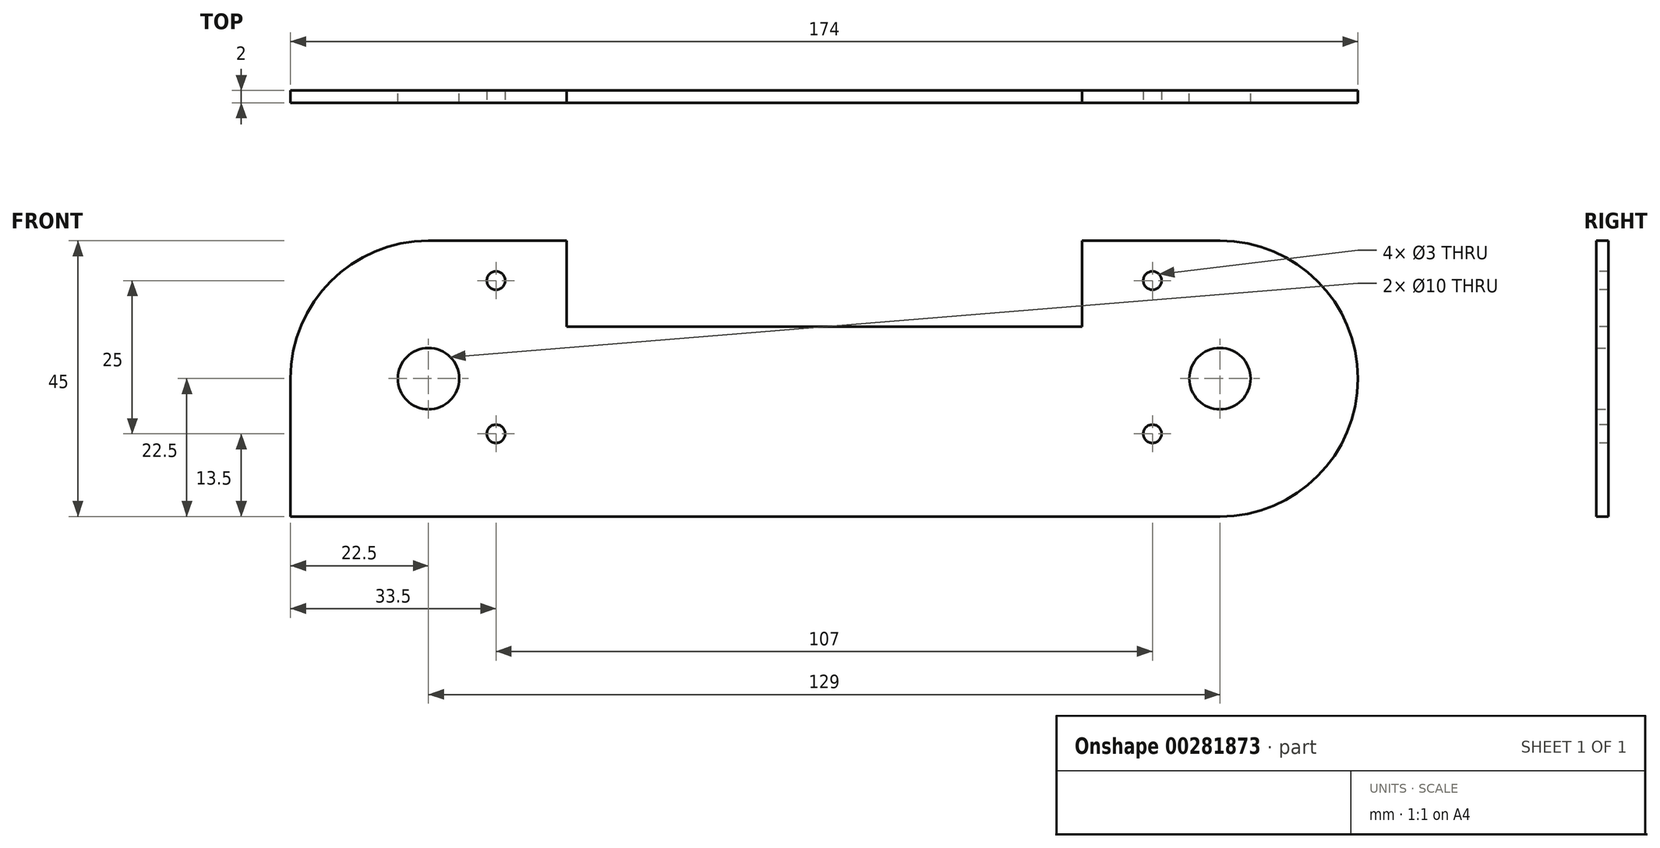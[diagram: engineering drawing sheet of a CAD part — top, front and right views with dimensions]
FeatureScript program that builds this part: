
annotation { "Feature Type Name" : "Feature", "Feature Type Description" : "" }
export const myFeature = defineFeature(function(context is Context, id is Id, definition is map)
    precondition{}
    {
        {
            var Q0;
            Q0=qCreatedBy(makeId("Front.planeOp"),FACE);
            var sketch = newSketch(context, id + "F0", { "sketchPlane" : qUnion([Q0])});
            skLineSegment(sketch, "E0.bottom", {"start": v(64.5, 22.5) * mm, "end": v(-64.5, 22.5) * mm});
            skLineSegment(sketch, "E0.top", {"start": v(64.5, -22.5) * mm, "end": v(-64.5, -22.5) * mm});
            skPoint(sketch, "E0.middle", {"position": v(0, 0) * mm});
            skCircle(sketch, "E1", {"center": v(64.5, 0) * mm, "radius": 5 * mm});
            skCircle(sketch, "E2", {"center": v(-64.5, 0) * mm, "radius": 5 * mm});
            skArc(sketch, "E3", {"start": v(-64.5, 22.5) * mm, "mid": v(-87, 0) * mm, "end": v(-64.5, -22.5) * mm});
            skArc(sketch, "E4", {"start": v(64.5, -22.5) * mm, "mid": v(87, 0) * mm, "end": v(64.5, 22.5) * mm});
            skPoint(sketch, "E5.orphan", {"position": v(-81.5, 22.5) * mm});
            skPoint(sketch, "E6.orphan", {"position": v(-81.5, -22.5) * mm});
            skPoint(sketch, "E7.orphan", {"position": v(81.5, 22.5) * mm});
            skPoint(sketch, "E8.orphan", {"position": v(81.5, -22.5) * mm});
            skSolve(sketch);
        }
        {
            var Q0;
            Q0=qSketchRegion(id+"F0",true);
            extrude(context, id + "F1", {"entities" : qUnion([Q0]), "depth" : 2 * mm});
        }
        {
            var Q0;
            Q0=makeQuery(id+"F1.opExtrude","CAP_FACE",FACE,{"disambiguationData":[OSD([sQuery(id+"F0.wireOp",EDGE,"E0.bottom"),sQuery(id+"F0.wireOp",EDGE,"E0.top"),sQuery(id+"F0.wireOp",EDGE,"E1"),sQuery(id+"F0.wireOp",EDGE,"E2"),sQuery(id+"F0.wireOp",EDGE,"E3"),sQuery(id+"F0.wireOp",EDGE,"E4")])],"isStart":false});
            var sketch = newSketch(context, id + "F2", { "sketchPlane" : qUnion([Q0])});
            skLineSegment(sketch, "E9.top", {"start": v(-64.5, -22.5) * mm, "end": v(-87, -22.5) * mm});
            skLineSegment(sketch, "E9.right", {"start": v(-87, 0) * mm, "end": v(-87, -22.5) * mm});
            skPoint(sketch, "E9.left.start.orphan", {"position": v(-64.5, 0) * mm});
            skLineSegment(sketch, "E10", {"start": v(-87, 0) * mm, "end": v(-80.88, 0) * mm});
            skLineSegment(sketch, "E11", {"start": v(-80.88, 0) * mm, "end": v(-78.27, -9.46) * mm});
            skLineSegment(sketch, "E12", {"start": v(-78.27, -9.46) * mm, "end": v(-70.55, -14.76) * mm});
            skLineSegment(sketch, "E13", {"start": v(-70.55, -14.76) * mm, "end": v(-64.5, -17.43) * mm});
            skLineSegment(sketch, "E14", {"start": v(-64.5, -17.43) * mm, "end": v(-64.5, -22.5) * mm});
            skSolve(sketch);
        }
        {
            var Q0;
            Q0=qSketchRegion(id+"F2",true);
            extrude(context, id + "F3", {"entities" : qUnion([Q0]), "operationType" : NewBodyOperationType.ADD, "oppositeDirection" : true, "depth" : 2 * mm});
        }
        {
            var Q0;
            Q0=makeQuery(id+"F3.boolean.opBoolean","MERGE",FACE,{"derivedFrom":[makeQuery(id+"F1.opExtrude","CAP_FACE",FACE,{"disambiguationData":[OSD([sQuery(id+"F0.wireOp",EDGE,"E0.bottom"),sQuery(id+"F0.wireOp",EDGE,"E0.top"),sQuery(id+"F0.wireOp",EDGE,"E1"),sQuery(id+"F0.wireOp",EDGE,"E2"),sQuery(id+"F0.wireOp",EDGE,"E3"),sQuery(id+"F0.wireOp",EDGE,"E4")])],"isStart":false}),makeQuery(id+"F3.opExtrude","CAP_FACE",FACE,{"disambiguationData":[OSD([sQuery(id+"F2.wireOp",EDGE,"E9.top"),sQuery(id+"F2.wireOp",EDGE,"E9.right"),sQuery(id+"F2.wireOp",EDGE,"E10"),sQuery(id+"F2.wireOp",EDGE,"E11"),sQuery(id+"F2.wireOp",EDGE,"E12"),sQuery(id+"F2.wireOp",EDGE,"E13"),sQuery(id+"F2.wireOp",EDGE,"E14")])],"isStart":true})]});
            var sketch = newSketch(context, id + "F4", { "sketchPlane" : qUnion([Q0])});
            skLineSegment(sketch, "E15.bottom", {"start": v(47, 22.5) * mm, "end": v(-47, 22.5) * mm, "construction": true});
            skLineSegment(sketch, "E15.top", {"start": v(47, -22.5) * mm, "end": v(-47, -22.5) * mm, "construction": true});
            skLineSegment(sketch, "E15.left", {"start": v(47, 22.5) * mm, "end": v(47, -22.5) * mm, "construction": true});
            skLineSegment(sketch, "E15.right", {"start": v(-47, 22.5) * mm, "end": v(-47, -22.5) * mm, "construction": true});
            skPoint(sketch, "E15.middle", {"position": v(0, 0) * mm});
            skLineSegment(sketch, "E16", {"start": v(-59.5, 0) * mm, "end": v(59.5, 0) * mm, "construction": true});
            skCircle(sketch, "E17", {"center": v(-53.5, 16) * mm, "radius": 1.5 * mm});
            skCircle(sketch, "E18", {"center": v(-53.5, -9) * mm, "radius": 1.5 * mm});
            skCircle(sketch, "E19", {"center": v(53.5, 16) * mm, "radius": 1.5 * mm});
            skCircle(sketch, "E20", {"center": v(53.5, -9) * mm, "radius": 1.5 * mm});
            skSolve(sketch);
        }
        {
            var Q0;
            Q0=qSketchRegion(id+"F4",true);
            extrude(context, id + "F5", {"entities" : qUnion([Q0]), "operationType" : NewBodyOperationType.REMOVE, "oppositeDirection" : true, "depth" : 25 * mm});
        }
        {
            var Q0;
            Q0=makeQuery(id+"F3.boolean.opBoolean","MERGE",FACE,{"derivedFrom":[makeQuery(id+"F1.opExtrude","CAP_FACE",FACE,{"disambiguationData":[OSD([sQuery(id+"F0.wireOp",EDGE,"E0.bottom"),sQuery(id+"F0.wireOp",EDGE,"E0.top"),sQuery(id+"F0.wireOp",EDGE,"E1"),sQuery(id+"F0.wireOp",EDGE,"E2"),sQuery(id+"F0.wireOp",EDGE,"E3"),sQuery(id+"F0.wireOp",EDGE,"E4")])],"isStart":false}),makeQuery(id+"F3.opExtrude","CAP_FACE",FACE,{"disambiguationData":[OSD([sQuery(id+"F2.wireOp",EDGE,"E9.top"),sQuery(id+"F2.wireOp",EDGE,"E9.right"),sQuery(id+"F2.wireOp",EDGE,"E10"),sQuery(id+"F2.wireOp",EDGE,"E11"),sQuery(id+"F2.wireOp",EDGE,"E12"),sQuery(id+"F2.wireOp",EDGE,"E13"),sQuery(id+"F2.wireOp",EDGE,"E14")])],"isStart":true})]});
            var sketch = newSketch(context, id + "F6", { "sketchPlane" : qUnion([Q0])});
            skLineSegment(sketch, "E21.bottom", {"start": v(42, 36.5) * mm, "end": v(-42, 36.5) * mm});
            skLineSegment(sketch, "E21.top", {"start": v(42, 8.5) * mm, "end": v(-42, 8.5) * mm});
            skLineSegment(sketch, "E21.left", {"start": v(42, 36.5) * mm, "end": v(42, 8.5) * mm});
            skLineSegment(sketch, "E21.right", {"start": v(-42, 36.5) * mm, "end": v(-42, 8.5) * mm});
            skPoint(sketch, "E21.middle", {"position": v(0, 22.5) * mm});
            skSolve(sketch);
        }
        {
            var Q0;
            Q0=qSketchRegion(id+"F6",true);
            extrude(context, id + "F7", {"entities" : qUnion([Q0]), "operationType" : NewBodyOperationType.REMOVE, "oppositeDirection" : true, "depth" : 25 * mm});
        }
    });
